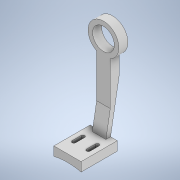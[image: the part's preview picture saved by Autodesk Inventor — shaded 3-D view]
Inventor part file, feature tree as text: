
AUTODESK INVENTOR PART (.ipt)
format: ipt  version: 2020.3 (Build 243373000, 373)  size: 404,480 bytes
history: native  units: in
note: dims shown in document units (in); Inventor stores cm internally (conversion verified against a paired STEP export)
features: sketch x20, extrude x8, thread x6, revolve x6, helix x6, other x5, plane x3, mirror x2, pattern_circular x1
ambient origin geometry x8: Origin, YZ Plane, XZ Plane, XY Plane, X Axis, Y Axis, Z Axis, Center Point
bodies: Solid1 (feature_tree), Solid3 (feature_tree), Solid4 (feature_tree), Solid5 (feature_tree), Solid6 (feature_tree), Solid7 (feature_tree), Solid8 (feature_tree)
feature tree (57):
  other  "Annotations"
  extrude  "Extrusion1"  Depth=0.75in
  extrude  "Extrusion2"  Depth=2.0in TaperAngle=0.0deg
  mirror  "Mirror1"
  extrude  "Extrusion3"  Depth=0.4in
  plane  "Work Plane1"
  extrude  "Extrusion4"  TaperAngle=0.0deg  [1 undecoded]
  extrude  "Extrusion5"  Depth=0.2in
  other  "Work Axis1"
  mirror  "Mirror4"
  extrude  "Extrusion6"  Depth=0.25in
  plane  "Work Plane3"
  extrude  "Extrusion7"  Depth=2.0in
  plane  "Work Plane4"
  extrude  "Extrusion9"  Depth=0.25in
  thread  "Thread2"  [1 undecoded]
  thread  "Thread3"  [1 undecoded]
  pattern_circular  "Circular Pattern1"  Count=3 Angle=360.0deg
  thread  "Thread4"  [1 undecoded]
  thread  "Thread5"  [1 undecoded]
  thread  "Thread6"  [1 undecoded]
  revolve  "Revolution2"  [1 undecoded]
  thread  "Thread7"  [1 undecoded]
  revolve  "Revolution3"  [1 undecoded]
  helix  "Coil2"  [1 undecoded]
  revolve  "Revolution4"  [1 undecoded]
  helix  "Coil3"  [1 undecoded]
  revolve  "Revolution5"  [1 undecoded]
  helix  "Coil4"  [1 undecoded]
  revolve  "Revolution6"  [1 undecoded]
  helix  "Coil5"  [1 undecoded]
  revolve  "Revolution7"  [1 undecoded]
  helix  "Coil6"  [1 undecoded]
  helix  "Coil7"  [1 undecoded]
  sketch  "Sketch1"  dims[d1=6.0in d2=0.75in]
  sketch  "Sketch2"  dims[d3=0.5in d4=2.0in d5=0.0in]
  sketch  "Sketch3"  dims[d6=0.0in d7=0.4in]
  sketch  "Sketch4"  dims[d8=0.25in d9=0.0in d10=0.0in]
  sketch  "Sketch7"  dims[d11=0.2in d13=2.75in]
  sketch  "Sketch8"  dims[d14=0.0687in d15=0.25in]
  sketch  "Sketch9"  dims[d16=0.75in d17=0.0in d18=2.0in]
  sketch  "Sketch14"  dims[d19=1.2in d20=0.25in d21=0.5in d22=0.0in d25=1.75in]
  sketch  "Sketch15"  dims[d26=0.75in d27=0.0in]
  sketch  "Sketch16"  dims[d31=0.75in d32=0.0in]
  sketch  "Sketch17"  dims[d38=0.125in d39=0.0in]
  sketch  "Sketch18"  dims[d62=0.0039in]
  sketch  "Sketch19"  dims[d64=60.0deg]
  sketch  "Sketch20"  dims[d74=0.159in]
  sketch  "Sketch21"  dims[d75=0.25in]
  sketch  "Sketch22"  dims[d76=0.25in]
  sketch  "Sketch23"  dims[d77=1.0in d78=0.0in]
  sketch  "Sketch24"  dims[d79=0.255in d80=0.0in]
  sketch  "Sketch25"  dims[d81=0.255in d82=0.0in d83=1.1811in d84=360.0deg d86=0.255in d87=0.0in d88=0.255in d89=0.0in d90=0.255in d91=0.0in]
  sketch  "Sketch26"  dims[d92=0.255in d93=0.0in d94=0.3779in d95=0.005in d96=0.005in d99=0.0312in d101=0.3779in d103=0.0in d104=0.0313in d105=0.3178in d106=0.3937in d107=0.0in d108=0.0in d109=0.0in d110=0.0in d111=0.0in d112=0.3779in d113=0.005in d114=0.005in d117=0.0312in d119=0.3779in d121=0.0in d122=0.0313in d123=0.3178in d124=0.3937in d125=0.0in d126=0.0in d127=0.0in d128=0.0in d129=0.0in d130=0.3779in d131=0.005in d132=0.005in d135=0.0312in d137=0.3779in d139=0.0in d140=0.0313in d141=0.3178in d142=0.3937in d143=0.0in d144=0.0in d145=0.0in d146=0.0in d147=0.0in d148=0.3779in d149=0.005in d150=0.005in d153=0.0312in d155=0.3779in d157=0.0in d158=0.0313in d159=0.3178in d160=0.3937in d161=0.0in d162=0.0in d163=0.0in d164=0.0in d165=0.0in d166=0.3779in d167=0.005in d168=0.005in d171=0.0312in d173=0.3779in d175=0.0in d176=0.0313in d177=0.3178in d178=0.3937in d179=0.0in d180=0.0in d181=0.0in d182=0.0in d183=0.0in d184=0.3779in d185=0.005in d186=0.005in d189=0.0312in d191=0.3779in d193=0.0in d194=0.0313in d195=0.3178in d196=0.3937in d197=0.0in d198=0.0in d199=0.0in d200=0.0in d201=0.0in d33=-0.1818in d34=5.0in d35=2.9698in d36=1.1814in d37=1.2in d28=0.5in d29=0.0344in]
  other  "Linear Dimension 1"
  other  "Linear Dimension 2"
  other  "Diameter Dimension 1"
note: 19 required parameter values undecoded (feature->parameter linkage not recoverable at this tier; creation-order binding heuristic only, values carry confidence <= 0.55)